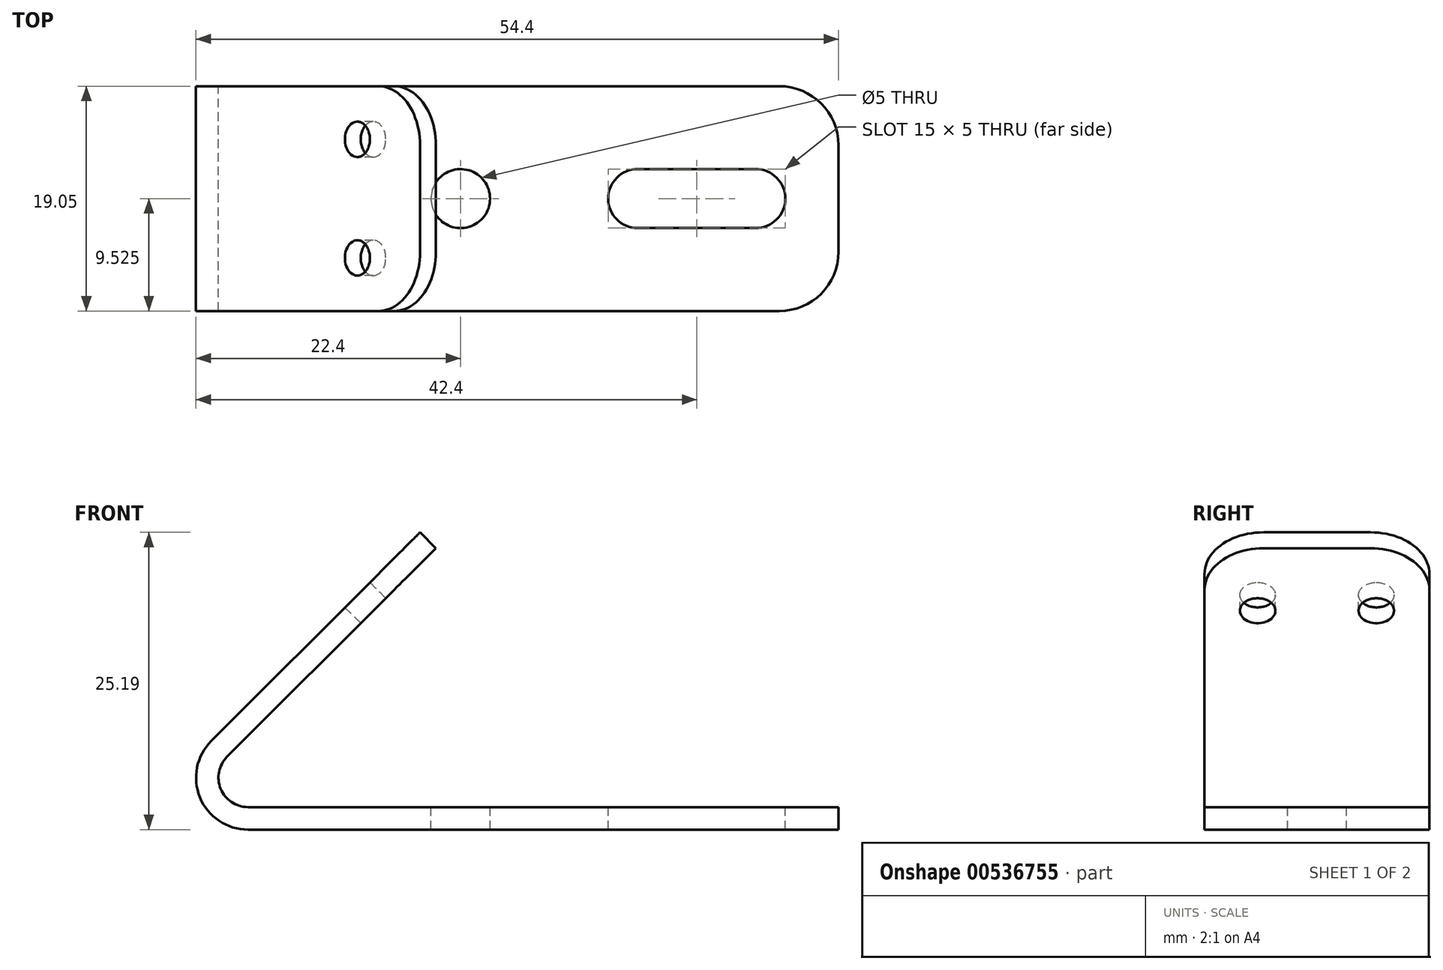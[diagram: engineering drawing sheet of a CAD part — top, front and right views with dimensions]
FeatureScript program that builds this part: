
annotation { "Feature Type Name" : "Feature", "Feature Type Description" : "" }
export const myFeature = defineFeature(function(context is Context, id is Id, definition is map)
    precondition{}
    {
        {
            var Q0;
            Q0=qCreatedBy(makeId("Front.planeOp"),FACE);
            var sketch = newSketch(context, id + "F0", { "sketchPlane" : qUnion([Q0])});
            skLineSegment(sketch, "E0", {"start": v(0, 0) * mm, "end": v(-50, 0) * mm});
            skArc(sketch, "E1", {"start": v(-53.11, 7.51) * mm, "mid": v(-54.07, 2.72) * mm, "end": v(-50, 0) * mm});
            skLineSegment(sketch, "E2", {"start": v(-53.11, 7.51) * mm, "end": v(-35.43, 25.19) * mm});
            skLineSegment(sketch, "E3", {"start": v(-35.43, 25.19) * mm, "end": v(-34.1, 23.85) * mm});
            skLineSegment(sketch, "E4", {"start": v(-34.1, 23.85) * mm, "end": v(-51.77, 6.17) * mm});
            skLineSegment(sketch, "E5", {"start": v(0, 0) * mm, "end": v(0, 1.9) * mm});
            skLineSegment(sketch, "E6", {"start": v(0, 1.9) * mm, "end": v(-50, 1.9) * mm});
            skArc(sketch, "E7", {"start": v(-51.77, 6.17) * mm, "mid": v(-52.3, 3.44) * mm, "end": v(-50, 1.9) * mm});
            skSolve(sketch);
        }
        {
            var Q0;
            Q0=makeQuery(id+"F0.imprint","IMPRINT",FACE,{"disambiguationData":[TD([[makeQuery(id+"F0.imprint","IMPRINT",EDGE,{"derivedFrom":sQuery(id+"F0.wireOp",EDGE,"E0")}),-1.0]])]});
            extrude(context, id + "F1", {"entities" : qUnion([Q0]), "depth" : 19.05 * mm, "offsetDistance" : 25 * mm});
        }
        {
            var Q0;
            Q0=makeQuery(id+"F1.opExtrude","SWEPT_FACE",FACE,{"disambiguationData":[OSD([sQuery(id+"F0.wireOp",EDGE,"E6")])]});
            var sketch = newSketch(context, id + "F2", { "sketchPlane" : qUnion([Q0])});
            skCircle(sketch, "E8", {"center": v(-32, -9.53) * mm, "radius": 2.5 * mm});
            skArc(sketch, "E9", {"start": v(-7, -12.03) * mm, "mid": v(-4.5, -9.53) * mm, "end": v(-7, -7.03) * mm});
            skArc(sketch, "E10", {"start": v(-17, -7.03) * mm, "mid": v(-19.5, -9.53) * mm, "end": v(-17, -12.03) * mm});
            skLineSegment(sketch, "E11", {"start": v(-17, -7.03) * mm, "end": v(-7, -7.03) * mm});
            skLineSegment(sketch, "E12", {"start": v(-17, -12.03) * mm, "end": v(-7, -12.03) * mm});
            skSolve(sketch);
        }
        {
            var Q0;
            Q0 = qSketchRegion(id + "F2", true);
            extrude(context, id + "F3", {"entities" : qUnion([Q0]), "operationType" : NewBodyOperationType.REMOVE, "oppositeDirection" : true, "depth" : 1.9 * mm, "offsetDistance" : 25 * mm});
        }
        {
            var Q0;
            Q0=makeQuery(id+"F1.opExtrude","SWEPT_FACE",FACE,{"disambiguationData":[OSD([sQuery(id+"F0.wireOp",EDGE,"E2")])]});
            var sketch = newSketch(context, id + "F4", { "sketchPlane" : qUnion([Q0])});
            skCircle(sketch, "E13", {"center": v(14.55, -14.74) * mm, "radius": 1.5 * mm});
            skCircle(sketch, "E14", {"center": v(4.5, -14.74) * mm, "radius": 1.5 * mm});
            skSolve(sketch);
        }
        {
            var Q0;
            Q0=makeQuery(id+"F4.imprint","IMPRINT",FACE,{"disambiguationData":[TD([[makeQuery(id+"F4.imprint","IMPRINT",EDGE,{"derivedFrom":sQuery(id+"F4.wireOp",EDGE,"E13")}),1.0]])]});
            var Q1;
            Q1=makeQuery(id+"F4.imprint","IMPRINT",FACE,{"disambiguationData":[TD([[makeQuery(id+"F4.imprint","IMPRINT",EDGE,{"derivedFrom":sQuery(id+"F4.wireOp",EDGE,"E14")}),1.0]])]});
            extrude(context, id + "F5", {"entities" : qUnion([Q0, Q1]), "operationType" : NewBodyOperationType.REMOVE, "oppositeDirection" : true, "depth" : 1.9 * mm, "offsetDistance" : 25 * mm});
        }
        {
            var Q0;
            Q0=makeQuery(id+"F1.opExtrude","CAP_EDGE",EDGE,{"disambiguationData":[OSD([sQuery(id+"F0.wireOp",EDGE,"E3")])],"isStart":true});
            var Q1;
            Q1=makeQuery(id+"F1.opExtrude","CAP_EDGE",EDGE,{"disambiguationData":[OSD([sQuery(id+"F0.wireOp",EDGE,"E3")])],"isStart":false});
            var Q2;
            Q2=makeQuery(id+"F1.opExtrude","CAP_EDGE",EDGE,{"disambiguationData":[OSD([sQuery(id+"F0.wireOp",EDGE,"E5")])],"isStart":false});
            var Q3;
            Q3=makeQuery(id+"F1.opExtrude","CAP_EDGE",EDGE,{"disambiguationData":[OSD([sQuery(id+"F0.wireOp",EDGE,"E5")])],"isStart":true});
            fillet(context, id + "F6", {"entities" : qUnion([Q0, Q1, Q2, Q3]), "radius" : 5 * mm, "tangentPropagation" : true, "allowEdgeOverflow" : false});
        }
    });
